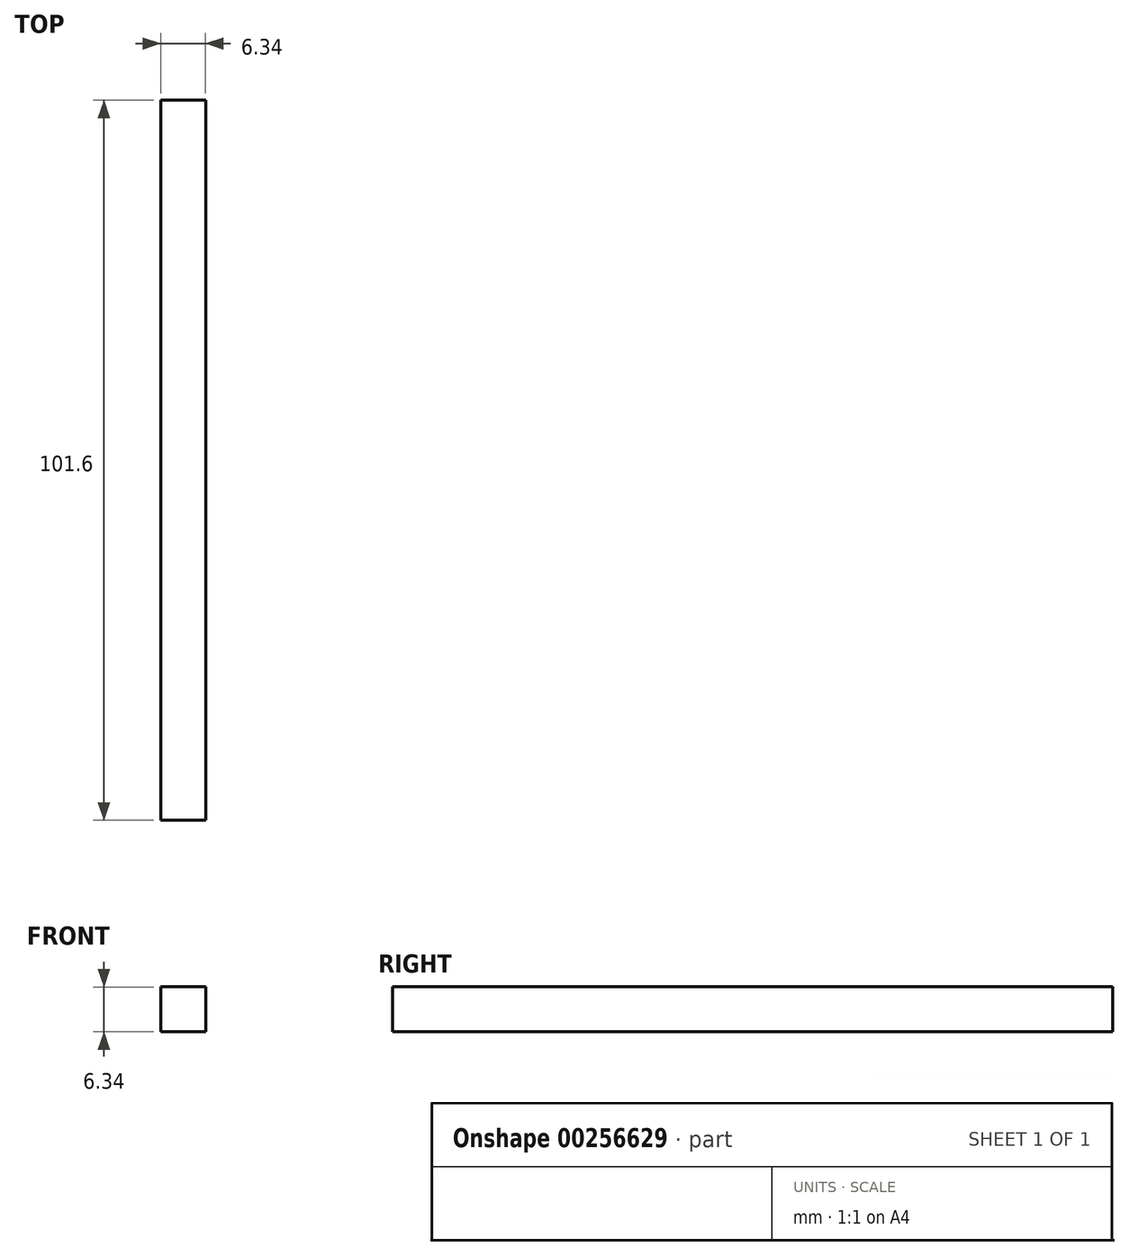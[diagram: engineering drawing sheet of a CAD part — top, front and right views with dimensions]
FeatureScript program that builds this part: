
annotation { "Feature Type Name" : "Feature", "Feature Type Description" : "" }
export const myFeature = defineFeature(function(context is Context, id is Id, definition is map)
    precondition{}
    {
        {
            var Q0;
            Q0=qCreatedBy(makeId("Front.planeOp"),FACE);
            var sketch = newSketch(context, id + "F0", { "sketchPlane" : qUnion([Q0])});
            skLineSegment(sketch, "E0.bottom", {"start": v(-3.18, 3.17) * mm, "end": v(3.18, 3.17) * mm});
            skLineSegment(sketch, "E0.top", {"start": v(-3.18, -3.18) * mm, "end": v(3.17, -3.18) * mm});
            skLineSegment(sketch, "E0.left", {"start": v(-3.18, 3.17) * mm, "end": v(-3.18, -3.18) * mm});
            skLineSegment(sketch, "E0.right", {"start": v(3.18, 3.17) * mm, "end": v(3.17, -3.18) * mm});
            skPoint(sketch, "E0.middle", {"position": v(0, 0) * mm});
            skSolve(sketch);
        }
        {
            var Q0;
            Q0=makeQuery(id+"F0.imprint","IMPRINT",FACE,{"disambiguationData":[TD([[makeQuery(id+"F0.imprint","IMPRINT",EDGE,{"derivedFrom":sQuery(id+"F0.wireOp",EDGE,"E0.bottom")}),-1.0]])]});
            extrude(context, id + "F1", {"entities" : qUnion([Q0]), "oppositeDirection" : true, "depth" : 101.6 * mm});
        }
    });
